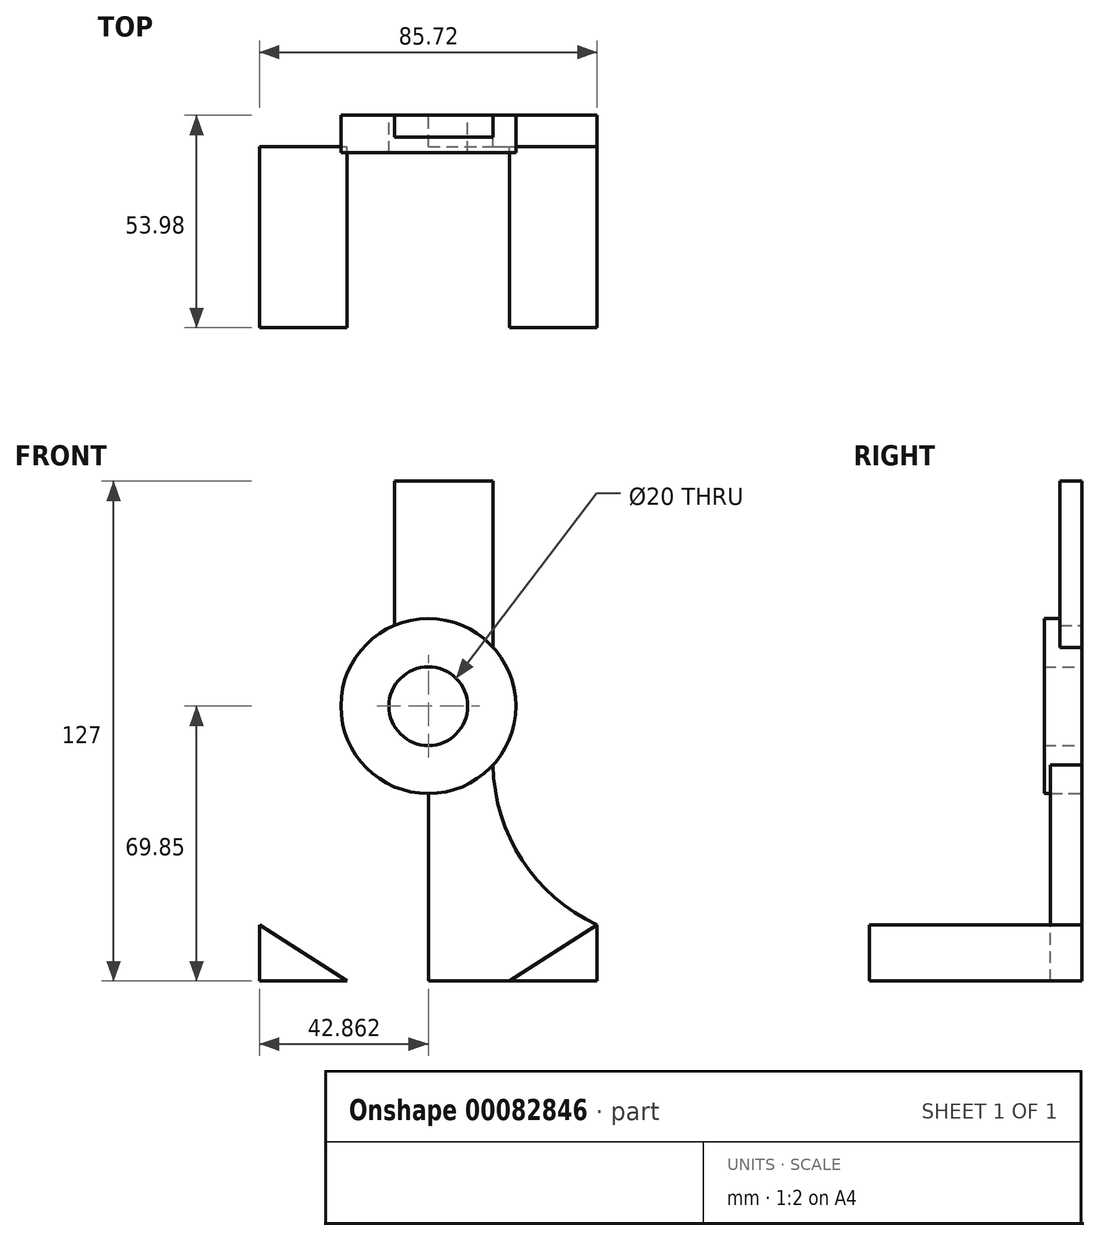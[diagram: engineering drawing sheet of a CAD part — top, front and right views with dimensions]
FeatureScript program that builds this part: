
annotation { "Feature Type Name" : "Feature", "Feature Type Description" : "" }
export const myFeature = defineFeature(function(context is Context, id is Id, definition is map)
    precondition{}
    {
        {
            var Q0;
            Q0=qCreatedBy(makeId("Front.planeOp"),FACE);
            var sketch = newSketch(context, id + "F0", { "sketchPlane" : qUnion([Q0])});
            skCircle(sketch, "E0", {"center": v(17.08, 69.85) * mm, "radius": 22.23 * mm});
            skCircle(sketch, "E1", {"center": v(17.08, 69.85) * mm, "radius": 10 * mm});
            skLineSegment(sketch, "E2", {"start": v(8.54, 69.85) * mm, "end": v(8.54, 127) * mm});
            skLineSegment(sketch, "E3", {"start": v(8.54, 127) * mm, "end": v(33.54, 127) * mm});
            skLineSegment(sketch, "E4", {"start": v(33.54, 127) * mm, "end": v(33.54, 0) * mm});
            skLineSegment(sketch, "E5", {"start": v(17.08, 69.85) * mm, "end": v(17.08, 0) * mm});
            skLineSegment(sketch, "E6.left", {"start": v(59.94, 0) * mm, "end": v(59.94, 14.29) * mm});
            skLineSegment(sketch, "E7", {"start": v(17.08, 0) * mm, "end": v(59.94, 0) * mm});
            skArc(sketch, "E8", {"start": v(33.54, 54.91) * mm, "mid": v(40.89, 30.8) * mm, "end": v(59.94, 14.29) * mm});
            skArc(sketch, "E9.MirrorCS", {"start": v(0.62, 54.91) * mm, "mid": v(-6.72, 30.8) * mm, "end": v(-25.78, 14.29) * mm});
            skLineSegment(sketch, "E10.MirrorCS", {"start": v(-25.78, 0) * mm, "end": v(-25.78, 14.29) * mm});
            skLineSegment(sketch, "E11.MirrorCS", {"start": v(17.08, 0) * mm, "end": v(-25.78, 0) * mm});
            skSolve(sketch);
        }
        {
            var Q0;
            {var subQ5=sQuery(id+"F0.wireOp",EDGE,"E3");Q0=makeQuery(id+"F0.imprint","IMPRINT",FACE,{"disambiguationData":[TD([[makeQuery(id+"F0.imprint","IMPRINT",EDGE,{"derivedFrom":subQ5}),-1.0]])]});}
            var Q1;
            {var subQ0=sQuery(id+"F0.wireOp",EDGE,"E2");var subQ1=sQuery(id+"F0.wireOp",EDGE,"E0");var subQ2=makeQuery(id+"F0.imprint","INTERSECT",VERTEX,{"derivedFrom":[subQ1,subQ0]});Q1=makeQuery(id+"F0.imprint","IMPRINT",FACE,{"disambiguationData":[TD([[makeQuery(id+"F0.imprint","IMPRINT",EDGE,{"disambiguationData":[TD([[subQ2,1.0]])],"derivedFrom":subQ1}),1.0]])]});}
            var Q2;
            {var subQ1=sQuery(id+"F0.wireOp",EDGE,"E0");var subQ7=makeQuery(id+"F0.imprint","INTERSECT",VERTEX,{"derivedFrom":[subQ1,sQuery(id+"F0.wireOp",EDGE,"E9.MirrorCS")]});Q2=makeQuery(id+"F0.imprint","IMPRINT",FACE,{"disambiguationData":[TD([[makeQuery(id+"F0.imprint","IMPRINT",EDGE,{"disambiguationData":[TD([[subQ7,1.0]])],"derivedFrom":subQ1}),1.0]])]});}
            var Q3;
            {var subQ0=sQuery(id+"F0.wireOp",EDGE,"E4");var subQ1=sQuery(id+"F0.wireOp",EDGE,"E0");var subQ3=makeQuery(id+"F0.imprint","INTERSECT",VERTEX,{"derivedFrom":[subQ1,subQ0]});Q3=makeQuery(id+"F0.imprint","IMPRINT",FACE,{"disambiguationData":[TD([[makeQuery(id+"F0.imprint","IMPRINT",EDGE,{"disambiguationData":[TD([[subQ3,1.0]])],"derivedFrom":subQ1}),1.0]])]});}
            var Q4;
            {var subQ0=sQuery(id+"F0.wireOp",EDGE,"E9.MirrorCS");Q4=makeQuery(id+"F0.imprint","IMPRINT",FACE,{"disambiguationData":[TD([[makeQuery(id+"F0.imprint","IMPRINT",EDGE,{"derivedFrom":subQ0}),1.0]])]});}
            var Q5;
            {var subQ1=sQuery(id+"F0.wireOp",EDGE,"E0");var subQ3=sQuery(id+"F0.wireOp",EDGE,"E5");var subQ4=makeQuery(id+"F0.imprint","INTERSECT",VERTEX,{"derivedFrom":[subQ1,subQ3]});Q5=makeQuery(id+"F0.imprint","IMPRINT",FACE,{"disambiguationData":[TD([[makeQuery(id+"F0.imprint","IMPRINT",EDGE,{"disambiguationData":[TD([[subQ4,-1.0]])],"derivedFrom":subQ1}),-1.0]])]});}
            var Q6;
            {var subQ4=sQuery(id+"F0.wireOp",EDGE,"E6.left");Q6=makeQuery(id+"F0.imprint","IMPRINT",FACE,{"disambiguationData":[TD([[makeQuery(id+"F0.imprint","IMPRINT",EDGE,{"derivedFrom":subQ4}),1.0]])]});}
            extrude(context, id + "F1", {"entities" : qUnion([Q0, Q1, Q2, Q3, Q4, Q5, Q6]), "depth" : 5.56 * mm});
        }
        {
            var Q0;
            Q0=makeQuery(id+"F1.opExtrude","CAP_FACE",FACE,{"disambiguationData":[OSD([sQuery(id+"F0.wireOp",EDGE,"E0"),sQuery(id+"F0.wireOp",EDGE,"E1"),sQuery(id+"F0.wireOp",EDGE,"E2"),sQuery(id+"F0.wireOp",EDGE,"E3"),sQuery(id+"F0.wireOp",EDGE,"E4"),sQuery(id+"F0.wireOp",EDGE,"E6.left"),sQuery(id+"F0.wireOp",EDGE,"E7"),sQuery(id+"F0.wireOp",EDGE,"E8"),sQuery(id+"F0.wireOp",EDGE,"E9.MirrorCS"),sQuery(id+"F0.wireOp",EDGE,"E10.MirrorCS"),sQuery(id+"F0.wireOp",EDGE,"E11.MirrorCS")])],"isStart":false});
            var sketch = newSketch(context, id + "F2", { "sketchPlane" : qUnion([Q0])});
            skCircle(sketch, "E12", {"center": v(17.08, 69.85) * mm, "radius": 22.23 * mm});
            skCircle(sketch, "E13", {"center": v(17.08, 69.85) * mm, "radius": 10 * mm});
            skSolve(sketch);
        }
        {
            var Q0;
            Q0 = qSketchRegion(id + "F2", true);
            extrude(context, id + "F3", {"entities" : qUnion([Q0]), "operationType" : NewBodyOperationType.ADD, "depth" : 3.97 * mm});
        }
        {
            var Q0;
            {var subQ0=sQuery(id+"F0.wireOp",EDGE,"E11.MirrorCS");var subQ1=sQuery(id+"F0.wireOp",EDGE,"E7");var subQ2=sQuery(id+"F0.wireOp",EDGE,"E6.left");var subQ3=sQuery(id+"F0.wireOp",EDGE,"E8");var subQ4=sQuery(id+"F0.wireOp",EDGE,"E4");var subQ5=sQuery(id+"F0.wireOp",EDGE,"E0");var subQ6=sQuery(id+"F0.wireOp",EDGE,"E9.MirrorCS");var subQ7=sQuery(id+"F0.wireOp",EDGE,"E2");var subQ8=sQuery(id+"F0.wireOp",EDGE,"E10.MirrorCS");Q0=makeQuery(id+"F3.boolean.opBoolean","SPLIT",FACE,{"disambiguationData":[TD([makeQuery(id+"F1.opExtrude","SWEPT_FACE",FACE,{"disambiguationData":[OSD([subQ2])]})])],"derivedFrom":makeQuery(id+"F1.opExtrude","CAP_FACE",FACE,{"disambiguationData":[OSD([subQ5,sQuery(id+"F0.wireOp",EDGE,"E1"),subQ7,sQuery(id+"F0.wireOp",EDGE,"E3"),subQ4,subQ2,subQ1,subQ3,subQ6,subQ8,subQ0])],"isStart":false})});}
            var sketch = newSketch(context, id + "F4", { "sketchPlane" : qUnion([Q0])});
            skSolve(sketch);
        }
        {
            var Q0;
            Q0 = qSketchRegion(id + "F4", true);
            var Q1;
            {var subQ0=sQuery(id+"F0.wireOp",EDGE,"E11.MirrorCS");var subQ1=sQuery(id+"F0.wireOp",EDGE,"E7");var subQ2=sQuery(id+"F0.wireOp",EDGE,"E6.left");var subQ3=sQuery(id+"F0.wireOp",EDGE,"E8");var subQ4=sQuery(id+"F0.wireOp",EDGE,"E4");var subQ5=sQuery(id+"F0.wireOp",EDGE,"E0");var subQ6=sQuery(id+"F0.wireOp",EDGE,"E9.MirrorCS");var subQ7=sQuery(id+"F0.wireOp",EDGE,"E2");var subQ8=sQuery(id+"F0.wireOp",EDGE,"E10.MirrorCS");Q1=makeQuery(id+"F3.boolean.opBoolean","SPLIT",FACE,{"disambiguationData":[TD([makeQuery(id+"F1.opExtrude","SWEPT_FACE",FACE,{"disambiguationData":[OSD([subQ2])]})])],"derivedFrom":makeQuery(id+"F1.opExtrude","CAP_FACE",FACE,{"disambiguationData":[OSD([subQ5,sQuery(id+"F0.wireOp",EDGE,"E1"),subQ7,sQuery(id+"F0.wireOp",EDGE,"E3"),subQ4,subQ2,subQ1,subQ3,subQ6,subQ8,subQ0])],"isStart":false})});}
            var Q2;
            {var subQ5=sQuery(id+"F0.wireOp",EDGE,"E6.left");Q2=makeQuery(id+"F4.imprint","IMPRINT",FACE,{"disambiguationData":[TD([[makeQuery(id+"F4.imprint","IMPRINT",EDGE,{"derivedFrom":makeQuery(id+"F1.opExtrude","CAP_EDGE",EDGE,{"disambiguationData":[OSD([subQ5])],"isStart":false})}),1.0]])]});}
            extrude(context, id + "F5", {"entities" : qUnion([Q0, Q1, Q2]), "operationType" : NewBodyOperationType.ADD, "depth" : 2.38 * mm});
        }
        {
            var Q0;
            Q0=makeQuery(id+"F5.opExtrude","CAP_FACE",FACE,{"disambiguationData":[OSD([sQuery(id+"F0.wireOp",EDGE,"E0"),sQuery(id+"F0.wireOp",EDGE,"E1"),sQuery(id+"F0.wireOp",EDGE,"E2"),sQuery(id+"F0.wireOp",EDGE,"E3"),sQuery(id+"F0.wireOp",EDGE,"E4"),sQuery(id+"F0.wireOp",EDGE,"E6.left"),sQuery(id+"F0.wireOp",EDGE,"E7"),sQuery(id+"F0.wireOp",EDGE,"E8"),sQuery(id+"F0.wireOp",EDGE,"E9.MirrorCS"),sQuery(id+"F0.wireOp",EDGE,"E10.MirrorCS"),sQuery(id+"F0.wireOp",EDGE,"E11.MirrorCS")])],"isStart":false});
            var sketch = newSketch(context, id + "F6", { "sketchPlane" : qUnion([Q0])});
            skLineSegment(sketch, "E14", {"start": v(-25.78, 0) * mm, "end": v(-25.78, 14.29) * mm});
            skLineSegment(sketch, "E15", {"start": v(59.94, 0) * mm, "end": v(59.94, 14.29) * mm});
            skLineSegment(sketch, "E16", {"start": v(-25.78, 0) * mm, "end": v(-3.56, 0) * mm});
            skLineSegment(sketch, "E17", {"start": v(59.94, 0) * mm, "end": v(37.72, 0) * mm});
            skLineSegment(sketch, "E18", {"start": v(-25.78, 14.29) * mm, "end": v(-3.56, 0) * mm});
            skLineSegment(sketch, "E19", {"start": v(37.72, 0) * mm, "end": v(59.94, 14.29) * mm});
            skSolve(sketch);
        }
        {
            var Q0;
            Q0=makeQuery(id+"F6.imprint","IMPRINT",FACE,{"disambiguationData":[TD([[makeQuery(id+"F6.imprint","IMPRINT",EDGE,{"derivedFrom":sQuery(id+"F6.wireOp",EDGE,"E14")}),-1.0]])]});
            var Q1;
            Q1=makeQuery(id+"F6.imprint","IMPRINT",FACE,{"disambiguationData":[TD([[makeQuery(id+"F6.imprint","IMPRINT",EDGE,{"derivedFrom":sQuery(id+"F6.wireOp",EDGE,"E15")}),1.0]])]});
            extrude(context, id + "F7", {"entities" : qUnion([Q0, Q1]), "operationType" : NewBodyOperationType.ADD, "depth" : 46.04 * mm});
        }
    });
